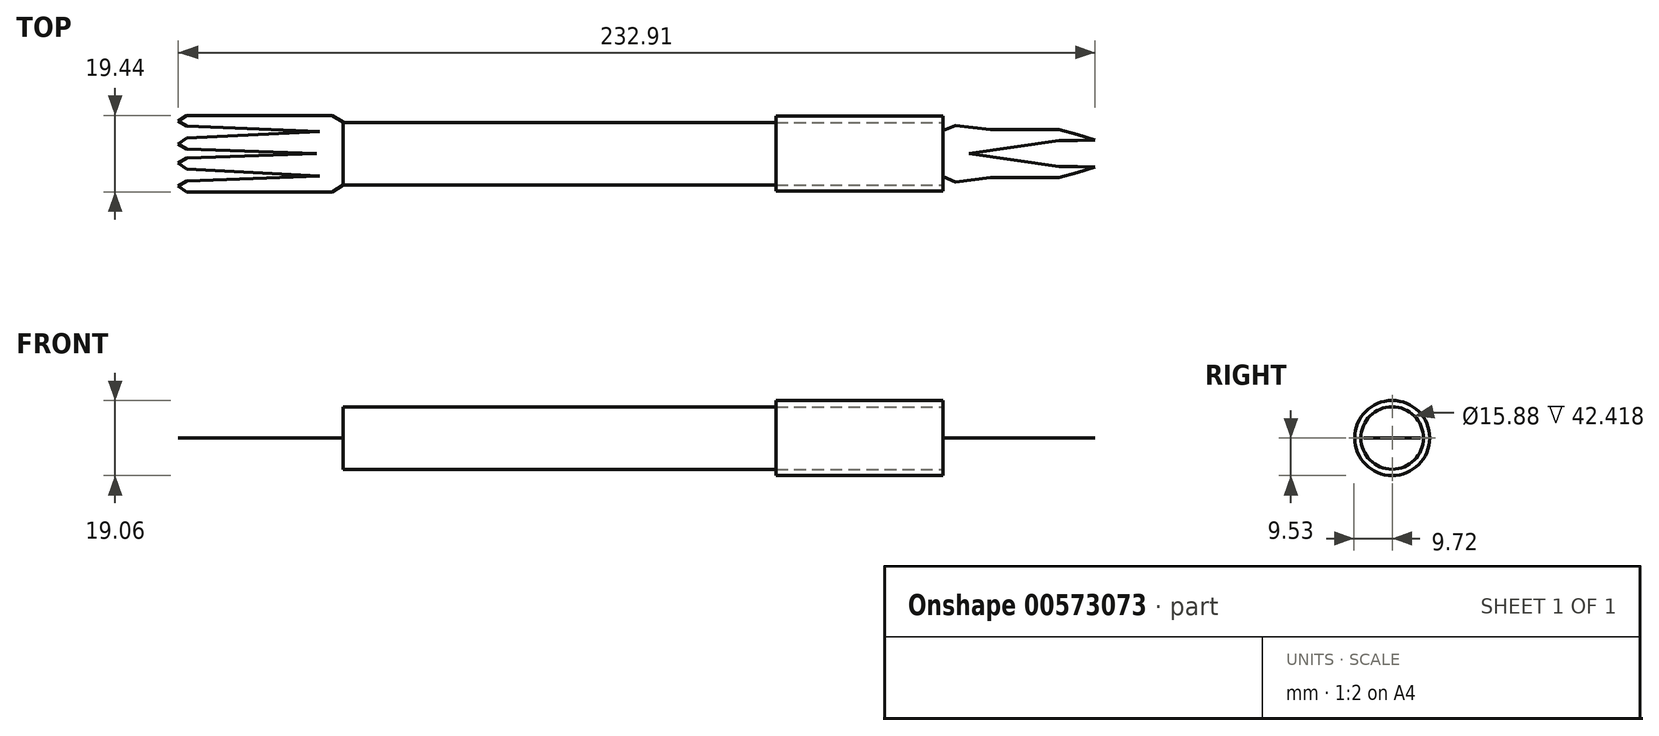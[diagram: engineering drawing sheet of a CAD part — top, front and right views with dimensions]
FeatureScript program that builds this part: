
annotation { "Feature Type Name" : "Feature", "Feature Type Description" : "" }
export const myFeature = defineFeature(function(context is Context, id is Id, definition is map)
    precondition{}
    {
        {
            var Q0;
            Q0=qCreatedBy(makeId("Right.planeOp"),FACE);
            var sketch = newSketch(context, id + "F0", { "sketchPlane" : qUnion([Q0])});
            skCircle(sketch, "E0", {"center": v(0, 0) * mm, "radius": 7.94 * mm});
            skSolve(sketch);
        }
        {
            var Q0;
            Q0 = qSketchRegion(id + "F0", true);
            var Q1;
            Q1 = qSketchRegion(id + "F4", true);
            extrude(context, id + "F1", {"entities" : qUnion([Q0, Q1]), "depth" : 152.4 * mm, "offsetDistance" : 25.4 * mm});
        }
        {
            var Q0;
            Q0=qCreatedBy(makeId("Top.planeOp"),FACE);
            var sketch = newSketch(context, id + "F2", { "sketchPlane" : qUnion([Q0])});
            skLineSegment(sketch, "E1", {"start": v(0, 7.98) * mm, "end": v(-2.77, 9.72) * mm});
            skLineSegment(sketch, "E2", {"start": v(-2.77, 9.72) * mm, "end": v(-39.77, 9.72) * mm});
            skLineSegment(sketch, "E3.MirrorCS", {"start": v(-2.77, -9.72) * mm, "end": v(-39.77, -9.72) * mm});
            skLineSegment(sketch, "E4.MirrorCS", {"start": v(0, -7.98) * mm, "end": v(-2.77, -9.72) * mm});
            skLineSegment(sketch, "E5", {"start": v(-39.77, -9.72) * mm, "end": v(-41.86, -8.25) * mm});
            skLineSegment(sketch, "E6", {"start": v(-41.86, -8.25) * mm, "end": v(-39.77, -6.96) * mm});
            skLineSegment(sketch, "E7", {"start": v(-39.77, -6.96) * mm, "end": v(-6, -5.68) * mm});
            skLineSegment(sketch, "E8.MirrorCS", {"start": v(-39.77, 6.96) * mm, "end": v(-6, 5.68) * mm});
            skLineSegment(sketch, "E9.MirrorCS", {"start": v(-41.86, 8.25) * mm, "end": v(-39.77, 6.96) * mm});
            skLineSegment(sketch, "E10.MirrorCS", {"start": v(-39.77, 9.72) * mm, "end": v(-41.86, 8.25) * mm});
            skLineSegment(sketch, "E11", {"start": v(-6, 5.68) * mm, "end": v(-39.77, 3.9) * mm});
            skLineSegment(sketch, "E12", {"start": v(-39.77, 3.9) * mm, "end": v(-41.86, 2.42) * mm});
            skLineSegment(sketch, "E13", {"start": v(-41.86, 2.42) * mm, "end": v(-39.77, 1.13) * mm});
            skLineSegment(sketch, "E14", {"start": v(-39.77, 1.13) * mm, "end": v(-6.74, 0) * mm});
            skLineSegment(sketch, "E15", {"start": v(0, 0) * mm, "end": v(-88.61, 0) * mm});
            skLineSegment(sketch, "E16.MirrorCS", {"start": v(-39.77, -1.13) * mm, "end": v(-6.74, 0) * mm});
            skLineSegment(sketch, "E17.MirrorCS", {"start": v(-6, -5.68) * mm, "end": v(-39.77, -3.9) * mm});
            skLineSegment(sketch, "E18.MirrorCS", {"start": v(-41.86, -2.42) * mm, "end": v(-39.77, -1.13) * mm});
            skLineSegment(sketch, "E19", {"start": v(0, 7.98) * mm, "end": v(0, -7.98) * mm});
            skLineSegment(sketch, "E20", {"start": v(-39.77, -3.9) * mm, "end": v(-41.86, -2.42) * mm});
            skSolve(sketch);
        }
        {
            var Q0;
            Q0 = qSketchRegion(id + "F2", true);
            extrude(context, id + "F3", {"entities" : qUnion([Q0]), "depth" : 1 / 406.4 * mm, "offsetDistance" : 25.4 * mm});
        }
        {
            var Q0;
            Q0=qCreatedBy(makeId("Top.planeOp"),FACE);
            var sketch = newSketch(context, id + "F4", { "sketchPlane" : qUnion([Q0])});
            skLineSegment(sketch, "E21", {"start": v(152.36, 5.8) * mm, "end": v(155.62, 7.16) * mm});
            skLineSegment(sketch, "E22", {"start": v(152.36, 5.8) * mm, "end": v(152.36, -6.01) * mm});
            skLineSegment(sketch, "E23", {"start": v(152.36, 0) * mm, "end": v(219.15, 0) * mm});
            skLineSegment(sketch, "E24", {"start": v(155.62, 7.16) * mm, "end": v(164.48, 6.08) * mm});
            skLineSegment(sketch, "E25", {"start": v(164.48, 6.08) * mm, "end": v(181.82, 6.08) * mm});
            skLineSegment(sketch, "E26", {"start": v(181.82, 6.08) * mm, "end": v(186.63, 4.84) * mm});
            skLineSegment(sketch, "E27", {"start": v(186.63, 4.84) * mm, "end": v(191.05, 3.41) * mm});
            skLineSegment(sketch, "E28", {"start": v(191.05, 3.41) * mm, "end": v(186.63, 3.3) * mm});
            skLineSegment(sketch, "E29", {"start": v(186.63, 3.3) * mm, "end": v(181.82, 3.3) * mm});
            skLineSegment(sketch, "E30", {"start": v(181.82, 3.3) * mm, "end": v(159, 0) * mm});
            skLineSegment(sketch, "E31.MirrorCS", {"start": v(181.82, -3.3) * mm, "end": v(159, 0) * mm});
            skLineSegment(sketch, "E32.MirrorCS", {"start": v(164.48, -6.08) * mm, "end": v(181.82, -6.08) * mm});
            skLineSegment(sketch, "E33.MirrorCS", {"start": v(155.62, -7.16) * mm, "end": v(164.48, -6.08) * mm});
            skLineSegment(sketch, "E34.MirrorCS", {"start": v(152.36, -5.8) * mm, "end": v(155.62, -7.16) * mm});
            skLineSegment(sketch, "E35.MirrorCS", {"start": v(186.63, -3.3) * mm, "end": v(181.82, -3.3) * mm});
            skLineSegment(sketch, "E36.MirrorCS", {"start": v(191.05, -3.41) * mm, "end": v(186.63, -3.3) * mm});
            skLineSegment(sketch, "E37.MirrorCS", {"start": v(186.63, -4.84) * mm, "end": v(191.05, -3.41) * mm});
            skLineSegment(sketch, "E38.MirrorCS", {"start": v(181.82, -6.08) * mm, "end": v(186.63, -4.84) * mm});
            skSolve(sketch);
        }
        {
            var Q0;
            Q0 = qSketchRegion(id + "F4", true);
            extrude(context, id + "F5", {"entities" : qUnion([Q0]), "operationType" : NewBodyOperationType.ADD, "depth" : 1 / 406.4 * mm, "offsetDistance" : 25.4 * mm});
        }
        {
            var Q0;
            Q0=makeQuery(id+"F1.opExtrude","CAP_FACE",FACE,{"disambiguationData":[OSD([sQuery(id+"F0.wireOp",EDGE,"E0")])],"isStart":false});
            var sketch = newSketch(context, id + "F6", { "sketchPlane" : qUnion([Q0])});
            skCircle(sketch, "E39", {"center": v(0, 0) * mm, "radius": 7.94 * mm});
            skCircle(sketch, "E40.0", {"center": v(0, 0) * mm, "radius": 9.53 * mm});
            skSolve(sketch);
        }
        {
            var Q0;
            Q0=makeQuery(id+"F6.imprint","IMPRINT",FACE,{"disambiguationData":[TD([[makeQuery(id+"F6.imprint","IMPRINT",EDGE,{"derivedFrom":sQuery(id+"F6.wireOp",EDGE,"E39")}),-1.0]])]});
            extrude(context, id + "F7", {"entities" : qUnion([Q0]), "oppositeDirection" : true, "depth" : 42.42 * mm, "offsetDistance" : 25.4 * mm});
        }
    });
